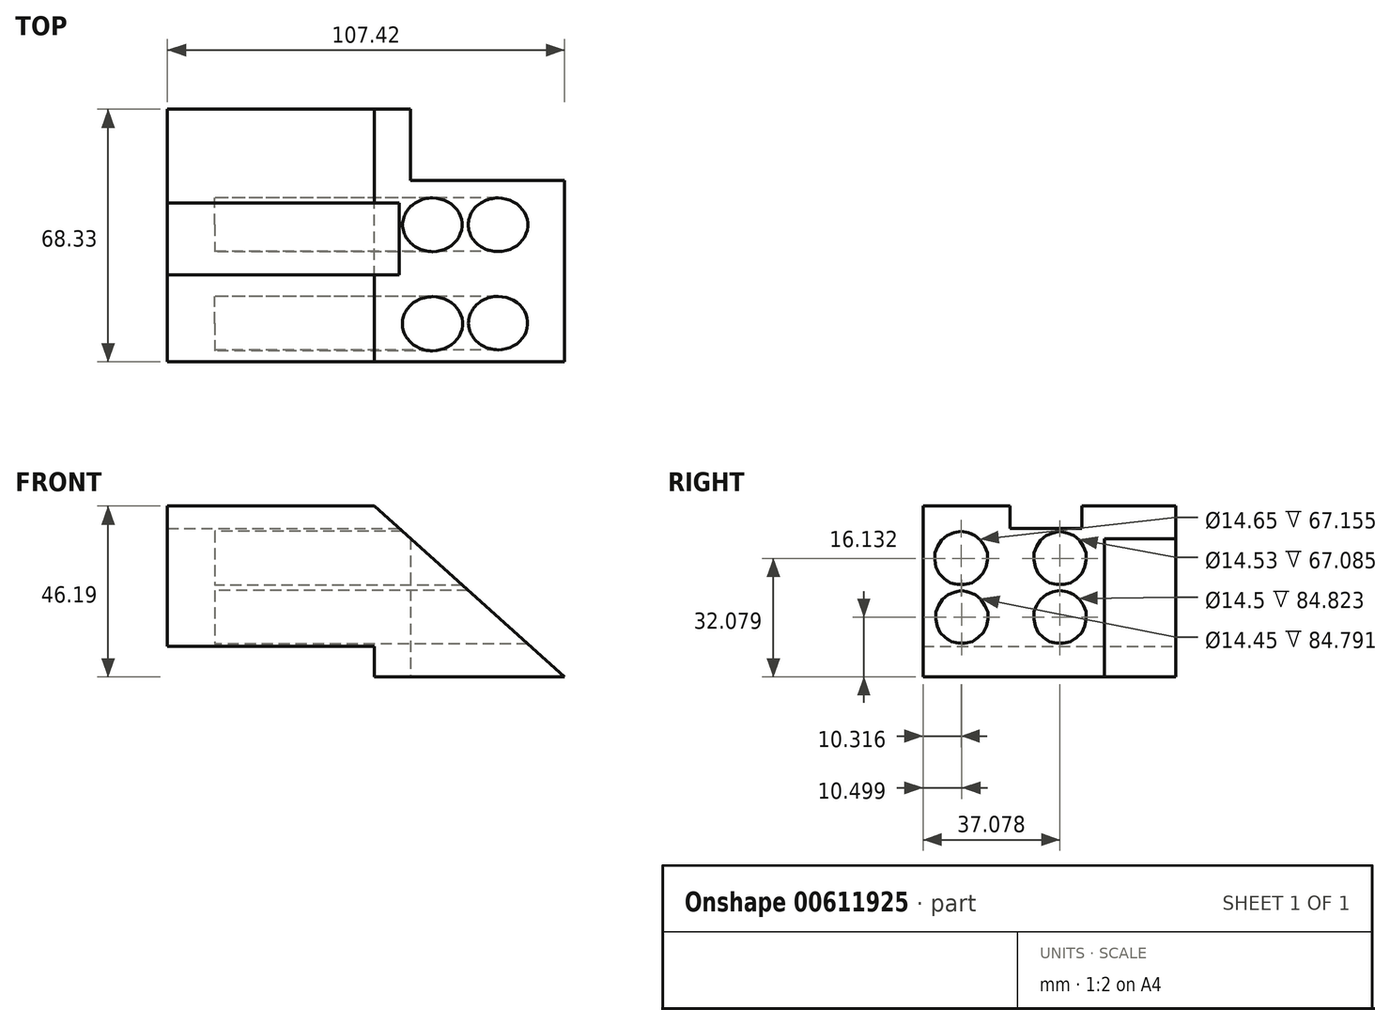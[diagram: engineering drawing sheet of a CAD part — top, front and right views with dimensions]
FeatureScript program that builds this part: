
annotation { "Feature Type Name" : "Feature", "Feature Type Description" : "" }
export const myFeature = defineFeature(function(context is Context, id is Id, definition is map)
    precondition{}
    {
        {
            var Q0;
            Q0=qCreatedBy(makeId("Front.planeOp"),FACE);
            var sketch = newSketch(context, id + "F0", { "sketchPlane" : qUnion([Q0])});
            skLineSegment(sketch, "E0", {"start": v(0, 37.94) * mm, "end": v(51.42, -8.25) * mm});
            skLineSegment(sketch, "E1", {"start": v(51.42, -8.25) * mm, "end": v(0, -8.25) * mm});
            skLineSegment(sketch, "E2", {"start": v(0, -8.25) * mm, "end": v(0, 0) * mm});
            skLineSegment(sketch, "E3", {"start": v(0, 0) * mm, "end": v(-56, 0) * mm});
            skLineSegment(sketch, "E4", {"start": v(0, 37.94) * mm, "end": v(-56, 37.94) * mm});
            skLineSegment(sketch, "E5", {"start": v(-56, 37.94) * mm, "end": v(-56, 0) * mm});
            skSolve(sketch);
        }
        {
            var Q0;
            Q0 = qSketchRegion(id + "F0", true);
            extrude(context, id + "F1", {"entities" : qUnion([Q0]), "depth" : 68.33 * mm, "offsetDistance" : 25.4 * mm});
        }
        {
            var Q0;
            Q0=qCreatedBy(makeId("Right.planeOp"),FACE);
            var sketch = newSketch(context, id + "F2", { "sketchPlane" : qUnion([Q0])});
            skLineSegment(sketch, "E6", {"start": v(-25.39, 38.3) * mm, "end": v(-25.39, 31.9) * mm});
            skLineSegment(sketch, "E7", {"start": v(-25.39, 31.9) * mm, "end": v(-44.82, 31.9) * mm});
            skLineSegment(sketch, "E8", {"start": v(-44.82, 31.9) * mm, "end": v(-44.82, 38.3) * mm});
            skLineSegment(sketch, "E9", {"start": v(-44.82, 38.3) * mm, "end": v(-25.39, 38.3) * mm});
            skSolve(sketch);
        }
        {
            var Q0;
            Q0 = qSketchRegion(id + "F2", true);
            extrude(context, id + "F3", {"entities" : qUnion([Q0]), "operationType" : NewBodyOperationType.REMOVE, "endBound" : BoundingType.SYMMETRIC, "oppositeDirection" : true, "depth" : 127 * mm, "offsetDistance" : 25.4 * mm});
        }
        {
            var Q0;
            Q0=qCreatedBy(makeId("Front.planeOp"),FACE);
            var sketch = newSketch(context, id + "F4", { "sketchPlane" : qUnion([Q0])});
            skLineSegment(sketch, "E10", {"start": v(51.42, -8.25) * mm, "end": v(9.8, 29.33) * mm});
            skLineSegment(sketch, "E11", {"start": v(9.8, 29.33) * mm, "end": v(9.8, -8.25) * mm});
            skLineSegment(sketch, "E12", {"start": v(9.8, -8.25) * mm, "end": v(51.42, -8.25) * mm});
            skSolve(sketch);
        }
        {
            var Q0;
            Q0 = qSketchRegion(id + "F4", true);
            extrude(context, id + "F5", {"entities" : qUnion([Q0]), "operationType" : NewBodyOperationType.REMOVE, "depth" : 19.3 * mm, "offsetDistance" : 25.4 * mm});
        }
        {
            var Q0;
            Q0=qCreatedBy(makeId("Right.planeOp"),FACE);
            var sketch = newSketch(context, id + "F6", { "sketchPlane" : qUnion([Q0])});
            skCircle(sketch, "E13", {"center": v(-58.01, 23.83) * mm, "radius": 7.33 * mm});
            skCircle(sketch, "E14", {"center": v(-31.25, 23.83) * mm, "radius": 7.26 * mm});
            skCircle(sketch, "E15", {"center": v(-31.25, 7.88) * mm, "radius": 7.25 * mm});
            skCircle(sketch, "E16", {"center": v(-57.83, 7.88) * mm, "radius": 7.22 * mm});
            skSolve(sketch);
        }
        {
            var Q0;
            Q0 = qSketchRegion(id + "F6", true);
            extrude(context, id + "F7", {"entities" : qUnion([Q0]), "operationType" : NewBodyOperationType.REMOVE, "endBound" : BoundingType.SYMMETRIC, "depth" : 86.36 * mm, "offsetDistance" : 25.4 * mm});
        }
    });
